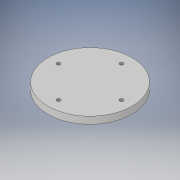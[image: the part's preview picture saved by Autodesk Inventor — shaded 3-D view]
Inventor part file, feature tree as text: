
AUTODESK INVENTOR PART (.ipt)
format: ipt  version: 2019 (Build 230136000, 136)  size: 138,240 bytes
history: native  units: in
note: dims shown in document units (in); Inventor stores cm internally (conversion verified against a paired STEP export)
features: extrude x5, sketch x5
ambient origin geometry x8: Origin, YZ Plane, XZ Plane, XY Plane, X Axis, Y Axis, Z Axis, Center Point
bodies: Solid1 (feature_tree)
feature tree (10):
  extrude  "Extrusion1"  Depth=0.76in
  extrude  "Extrusion2"  Depth=0.25in TaperAngle=0.0deg
  extrude  "Extrusion3"  Depth=0.1in TaperAngle=0.0deg
  extrude  "Extrusion4"  Depth=0.25in TaperAngle=0.0deg
  extrude  "Extrusion5"  Depth=0.25in
  sketch  "Sketch1"  dims[d0=1.0in d1=0.76in]
  sketch  "Sketch2"  dims[d2=3.0in d3=0.25in d4=0.0in]
  sketch  "Sketch3"  dims[d5=0.1in d6=0.0in d7=0.1in d8=0.0in]
  sketch  "Sketch4"  dims[d9=1.5in d10=0.25in d11=0.0in]
  sketch  "Sketch5"  dims[d12=0.125in d13=0.125in d14=0.125in d15=0.125in d16=0.25in d17=0.0in]
